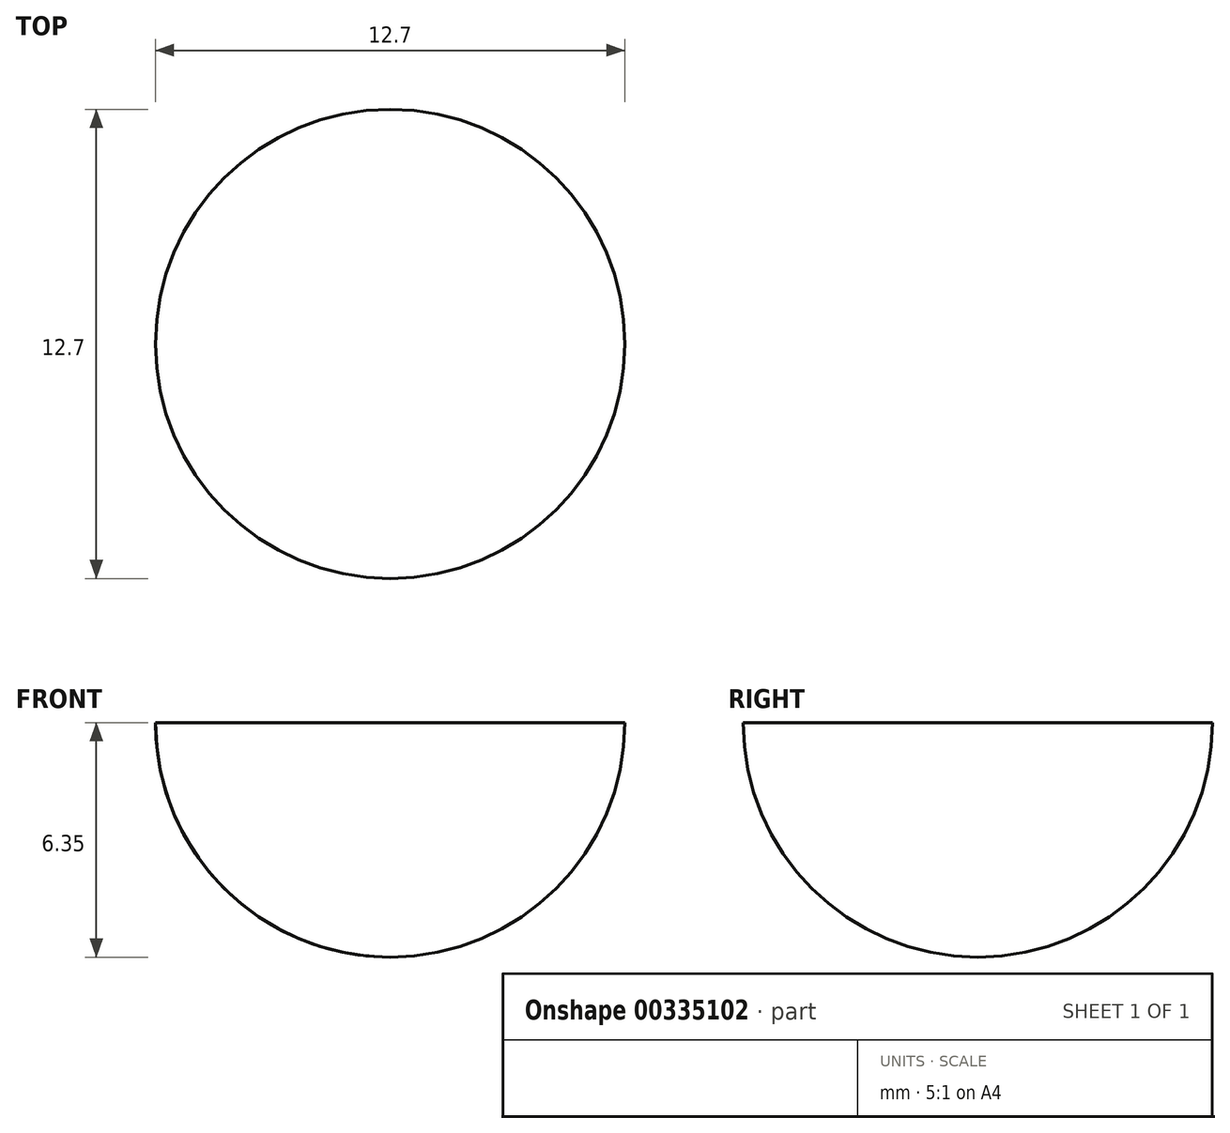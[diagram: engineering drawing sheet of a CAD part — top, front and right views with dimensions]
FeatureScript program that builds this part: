
annotation { "Feature Type Name" : "Feature", "Feature Type Description" : "" }
export const myFeature = defineFeature(function(context is Context, id is Id, definition is map)
    precondition{}
    {
        {
            var Q0;
            Q0=qCreatedBy(makeId("Front.planeOp"),FACE);
            var sketch = newSketch(context, id + "F0", { "sketchPlane" : qUnion([Q0])});
            skArc(sketch, "E0", {"start": v(0, -6.35) * mm, "mid": v(4.5, -4.5) * mm, "end": v(6.35, 0) * mm});
            skLineSegment(sketch, "E1", {"start": v(0, 0) * mm, "end": v(0, -6.35) * mm});
            skLineSegment(sketch, "E2", {"start": v(0, 0) * mm, "end": v(6.35, 0) * mm});
            skSolve(sketch);
        }
        {
            var Q0;
            Q0=makeQuery(id+"F0.imprint","IMPRINT",FACE,{"disambiguationData":[TD([[makeQuery(id+"F0.imprint","IMPRINT",EDGE,{"derivedFrom":sQuery(id+"F0.wireOp",EDGE,"E0")}),1.0]])]});
            var Q1;
            Q1=sQuery(id+"F0.wireOp",EDGE,"E1");
            revolve(context, id + "F1", {"entities" : qUnion([Q0]), "axis" : qUnion([Q1]), "revolveType" : RevolveType.FULL});
        }
    });
